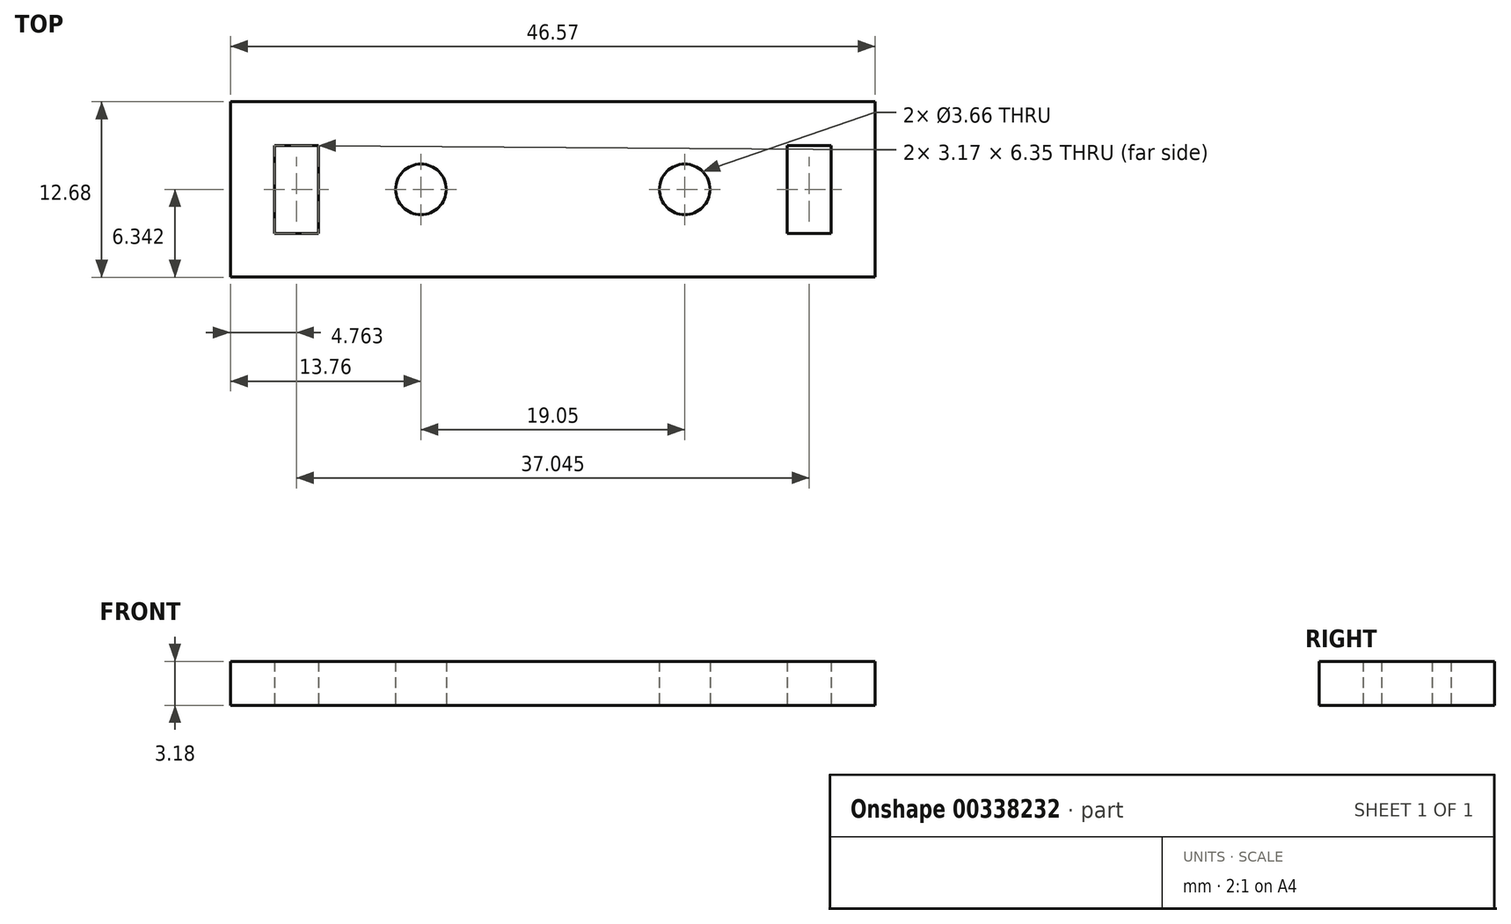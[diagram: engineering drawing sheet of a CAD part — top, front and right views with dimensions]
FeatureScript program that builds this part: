
annotation { "Feature Type Name" : "Feature", "Feature Type Description" : "" }
export const myFeature = defineFeature(function(context is Context, id is Id, definition is map)
    precondition{}
    {
        {
            var Q0;
            Q0=qCreatedBy(makeId("Top.planeOp"),FACE);
            var sketch = newSketch(context, id + "F0", { "sketchPlane" : qUnion([Q0])});
            skLineSegment(sketch, "E0.bottom", {"start": v(0, 0) * mm, "end": v(-46.57, 0) * mm});
            skLineSegment(sketch, "E0.top", {"start": v(0, -12.68) * mm, "end": v(-46.57, -12.68) * mm});
            skLineSegment(sketch, "E0.left", {"start": v(0, 0) * mm, "end": v(0, -12.68) * mm});
            skLineSegment(sketch, "E0.right", {"start": v(-46.57, 0) * mm, "end": v(-46.57, -12.68) * mm});
            skLineSegment(sketch, "E1.bottom", {"start": v(-3.18, -9.51) * mm, "end": v(-6.35, -9.51) * mm});
            skLineSegment(sketch, "E1.top", {"start": v(-3.18, -3.16) * mm, "end": v(-6.35, -3.16) * mm});
            skLineSegment(sketch, "E1.left", {"start": v(-3.18, -9.51) * mm, "end": v(-3.18, -3.16) * mm});
            skLineSegment(sketch, "E1.right", {"start": v(-6.35, -9.51) * mm, "end": v(-6.35, -3.16) * mm});
            skLineSegment(sketch, "E2.bottom", {"start": v(-43.4, -9.51) * mm, "end": v(-40.22, -9.51) * mm});
            skLineSegment(sketch, "E2.top", {"start": v(-43.4, -3.16) * mm, "end": v(-40.22, -3.16) * mm});
            skLineSegment(sketch, "E2.left", {"start": v(-43.4, -9.51) * mm, "end": v(-43.4, -3.16) * mm});
            skLineSegment(sketch, "E2.right", {"start": v(-40.22, -9.51) * mm, "end": v(-40.22, -3.16) * mm});
            skLineSegment(sketch, "E3", {"start": v(-43.4, -6.34) * mm, "end": v(-46.57, -6.34) * mm, "construction": true});
            skLineSegment(sketch, "E4", {"start": v(-3.18, -6.34) * mm, "end": v(0, -6.34) * mm, "construction": true});
            skCircle(sketch, "E5", {"center": v(-32.8, -6.34) * mm, "radius": 1.83 * mm});
            skLineSegment(sketch, "E6", {"start": v(-40.22, -6.34) * mm, "end": v(-32.8, -6.34) * mm, "construction": true});
            skLineSegment(sketch, "E7", {"start": v(-32.8, -6.34) * mm, "end": v(-13.76, -6.34) * mm, "construction": true});
            skLineSegment(sketch, "E8", {"start": v(-13.76, -6.34) * mm, "end": v(-6.35, -6.34) * mm, "construction": true});
            skCircle(sketch, "E9", {"center": v(-13.76, -6.34) * mm, "radius": 1.83 * mm});
            skSolve(sketch);
        }
        {
            var Q0;
            Q0 = qSketchRegion(id + "F0", true);
            extrude(context, id + "F1", {"entities" : qUnion([Q0]), "depth" : 3.17 * mm});
        }
    });
